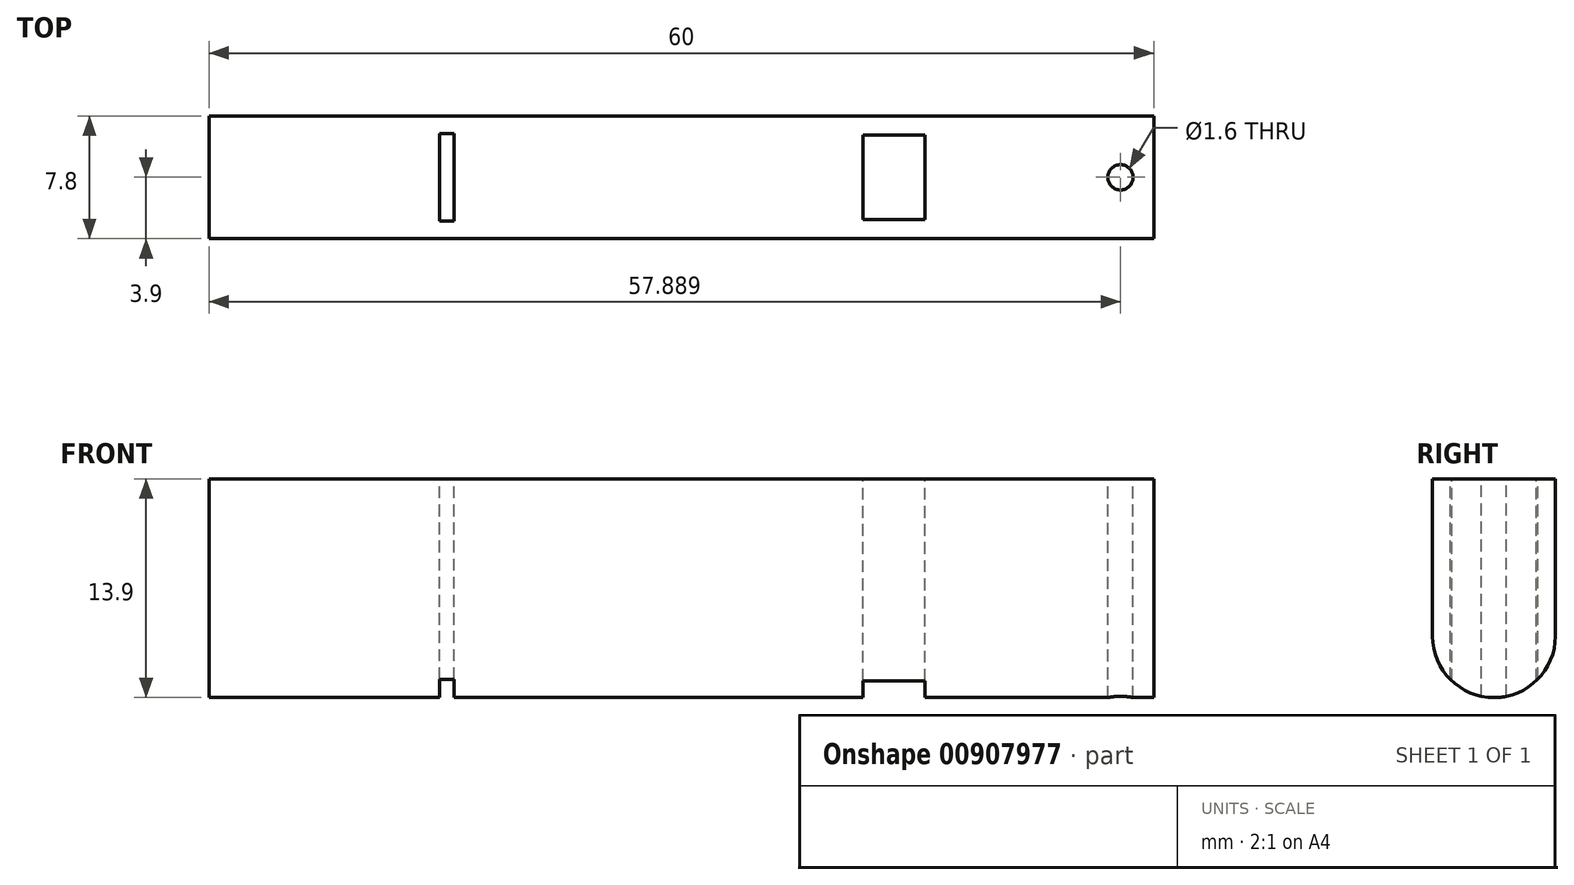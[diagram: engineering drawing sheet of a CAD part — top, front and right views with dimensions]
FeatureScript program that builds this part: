
annotation { "Feature Type Name" : "Feature", "Feature Type Description" : "" }
export const myFeature = defineFeature(function(context is Context, id is Id, definition is map)
    precondition{}
    {
        {
            var Q0;
            Q0=qCreatedBy(makeId("Right.planeOp"),FACE);
            var sketch = newSketch(context, id + "F0", { "sketchPlane" : qUnion([Q0])});
            skLineSegment(sketch, "E0.top", {"start": v(0, 10) * mm, "end": v(-3.9, 10) * mm});
            skLineSegment(sketch, "E0.right", {"start": v(-3.9, 0) * mm, "end": v(-3.9, 10) * mm});
            skLineSegment(sketch, "E1.MirrorCS", {"start": v(0, 10) * mm, "end": v(3.9, 10) * mm});
            skLineSegment(sketch, "E2.MirrorCS", {"start": v(3.9, 0) * mm, "end": v(3.9, 10) * mm});
            skArc(sketch, "E3", {"start": v(-3.9, 0) * mm, "mid": v(0, -3.9) * mm, "end": v(3.9, 0) * mm});
            skSolve(sketch);
        }
        {
            var Q0;
            Q0=makeQuery(id+"F0.imprint","IMPRINT",FACE,{"disambiguationData":[TD([[makeQuery(id+"F0.imprint","IMPRINT",EDGE,{"derivedFrom":sQuery(id+"F0.wireOp",EDGE,"E0.top")}),1.0]])]});
            extrude(context, id + "F1", {"entities" : qUnion([Q0]), "endBound" : BoundingType.SYMMETRIC, "depth" : 60 * mm, "offsetDistance" : 25 * mm});
        }
        {
            var Q0;
            Q0=makeQuery(id+"F1.opExtrude","SWEPT_FACE",FACE,{"disambiguationData":[OSD([sQuery(id+"F0.wireOp",EDGE,"E0.top"),sQuery(id+"F0.wireOp",EDGE,"E1.MirrorCS")])]});
            var sketch = newSketch(context, id + "F2", { "sketchPlane" : qUnion([Q0])});
            skLineSegment(sketch, "E4.bottom", {"start": v(-15.36, 2.78) * mm, "end": v(-14.43, 2.78) * mm});
            skLineSegment(sketch, "E4.top", {"start": v(-15.36, -2.78) * mm, "end": v(-14.43, -2.78) * mm});
            skLineSegment(sketch, "E4.left", {"start": v(-15.36, 2.78) * mm, "end": v(-15.36, -2.78) * mm});
            skLineSegment(sketch, "E4.right", {"start": v(-14.43, 2.78) * mm, "end": v(-14.43, -2.78) * mm});
            skPoint(sketch, "E4.middle", {"position": v(-14.9, 0) * mm});
            skSolve(sketch);
        }
        {
            var Q0;
            Q0=makeQuery(id+"F2.imprint","IMPRINT",FACE,{"disambiguationData":[TD([[makeQuery(id+"F2.imprint","IMPRINT",EDGE,{"derivedFrom":sQuery(id+"F2.wireOp",EDGE,"E4.bottom")}),1.0]])]});
            var sketch = newSketch(context, id + "F3", { "sketchPlane" : qUnion([Q0])});
            skLineSegment(sketch, "E5.bottom", {"start": v(11.52, 2.68) * mm, "end": v(15.47, 2.68) * mm});
            skLineSegment(sketch, "E5.top", {"start": v(11.52, -2.68) * mm, "end": v(15.47, -2.68) * mm});
            skLineSegment(sketch, "E5.left", {"start": v(11.52, 2.68) * mm, "end": v(11.52, -2.68) * mm});
            skLineSegment(sketch, "E5.right", {"start": v(15.47, 2.68) * mm, "end": v(15.47, -2.68) * mm});
            skPoint(sketch, "E5.middle", {"position": v(13.5, 0) * mm});
            skSolve(sketch);
        }
        {
            var Q0;
            Q0=makeQuery(id+"F2.imprint","IMPRINT",FACE,{"disambiguationData":[TD([[makeQuery(id+"F2.imprint","IMPRINT",EDGE,{"derivedFrom":sQuery(id+"F2.wireOp",EDGE,"E4.bottom")}),1.0]])]});
            var sketch = newSketch(context, id + "F4", { "sketchPlane" : qUnion([Q0])});
            skCircle(sketch, "E6", {"center": v(27.89, 0) * mm, "radius": 0.8 * mm});
            skSolve(sketch);
        }
        {
            var Q0;
            Q0=makeQuery(id+"F2.imprint","IMPRINT",FACE,{"disambiguationData":[TD([[makeQuery(id+"F2.imprint","IMPRINT",EDGE,{"derivedFrom":sQuery(id+"F2.wireOp",EDGE,"E4.bottom")}),-1.0]])]});
            extrude(context, id + "F5", {"entities" : qUnion([Q0]), "operationType" : NewBodyOperationType.REMOVE, "endBound" : BoundingType.THROUGH_ALL, "oppositeDirection" : true, "depth" : 25 * mm, "offsetDistance" : 25 * mm});
        }
        {
            var Q0;
            Q0=makeQuery(id+"F3.imprint","IMPRINT",FACE,{"disambiguationData":[TD([[makeQuery(id+"F3.imprint","IMPRINT",EDGE,{"derivedFrom":sQuery(id+"F3.wireOp",EDGE,"E5.bottom")}),-1.0]])]});
            extrude(context, id + "F6", {"entities" : qUnion([Q0]), "operationType" : NewBodyOperationType.REMOVE, "endBound" : BoundingType.THROUGH_ALL, "oppositeDirection" : true, "depth" : 25 * mm, "offsetDistance" : 25 * mm});
        }
        {
            var Q0;
            Q0=makeQuery(id+"F4.imprint","IMPRINT",FACE,{"disambiguationData":[TD([[makeQuery(id+"F4.imprint","IMPRINT",EDGE,{"derivedFrom":sQuery(id+"F4.wireOp",EDGE,"E6")}),1.0]])]});
            extrude(context, id + "F7", {"entities" : qUnion([Q0]), "operationType" : NewBodyOperationType.REMOVE, "endBound" : BoundingType.THROUGH_ALL, "oppositeDirection" : true, "depth" : 25 * mm, "offsetDistance" : 25 * mm});
        }
    });
